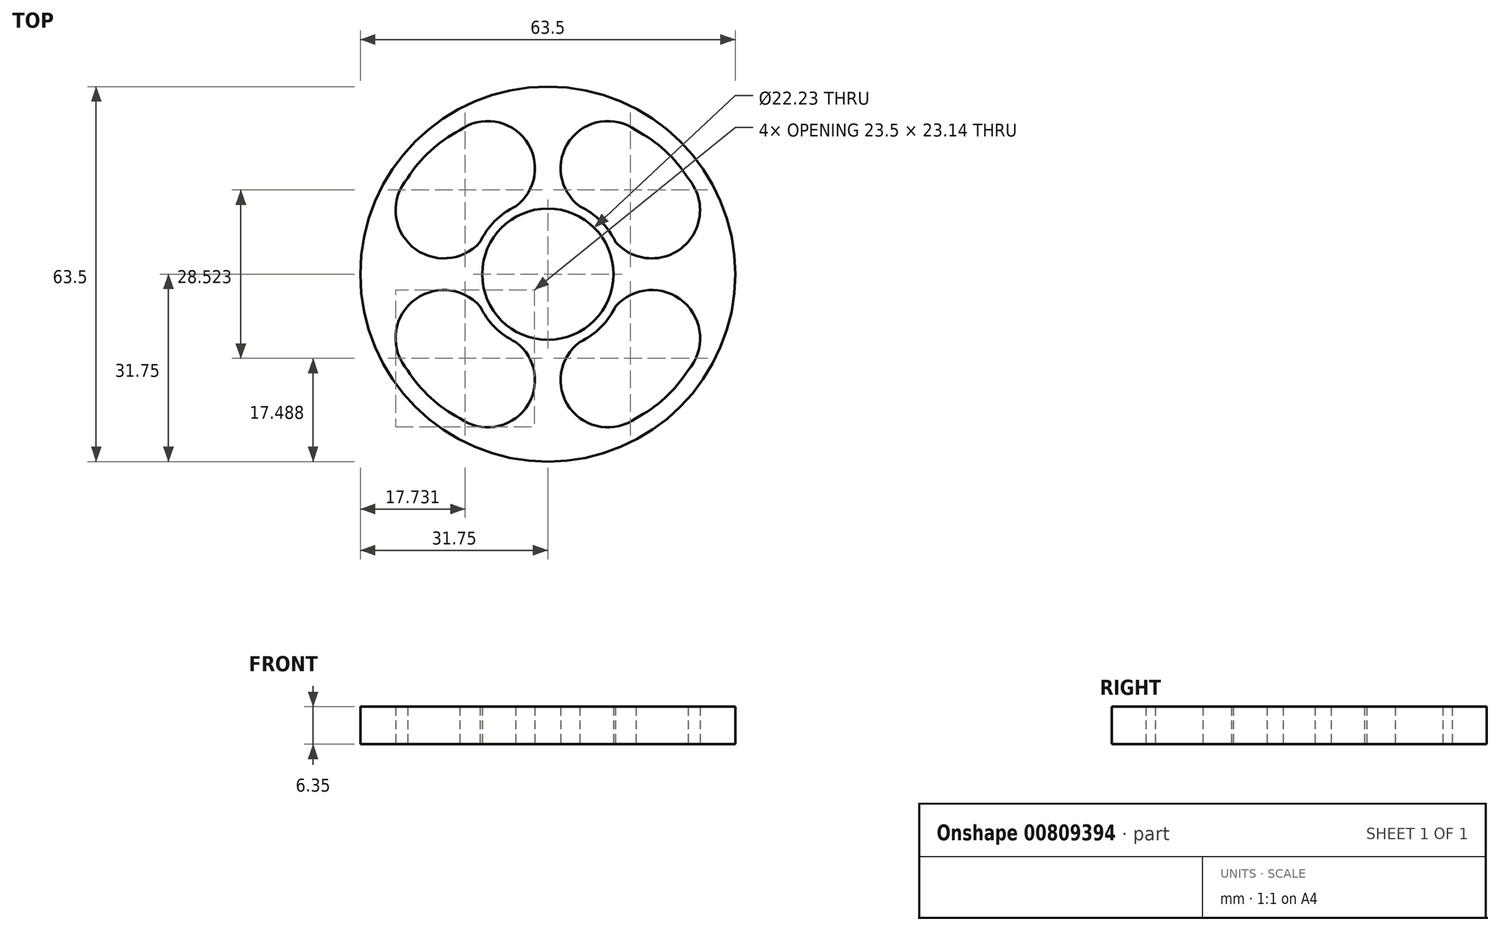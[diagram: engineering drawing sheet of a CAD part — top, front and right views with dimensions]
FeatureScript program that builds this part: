
annotation { "Feature Type Name" : "Feature", "Feature Type Description" : "" }
export const myFeature = defineFeature(function(context is Context, id is Id, definition is map)
    precondition{}
    {
        {
            var Q0;
            Q0=qCreatedBy(makeId("Top.planeOp"),FACE);
            var sketch = newSketch(context, id + "F0", { "sketchPlane" : qUnion([Q0])});
            skCircle(sketch, "E0", {"center": v(0, 0) * mm, "radius": 31.75 * mm});
            skCircle(sketch, "E1", {"center": v(0, 0) * mm, "radius": 11.11 * mm});
            skSolve(sketch);
        }
        {
            var Q0;
            Q0=makeQuery(id+"F0.imprint","IMPRINT",FACE,{"disambiguationData":[TD([[makeQuery(id+"F0.imprint","IMPRINT",EDGE,{"derivedFrom":sQuery(id+"F0.wireOp",EDGE,"E0")}),1.0]])]});
            extrude(context, id + "F1", {"entities" : qUnion([Q0]), "depth" : 6.35 * mm, "offsetDistance" : 25.4 * mm});
        }
        {
            var Q0;
            Q0=qCreatedBy(makeId("Top.planeOp"),FACE);
            var sketch = newSketch(context, id + "F2", { "sketchPlane" : qUnion([Q0])});
            skArc(sketch, "E2.MirrorCS", {"start": v(14.92, 24.37) * mm, "mid": v(3.73, 22.66) * mm, "end": v(5.44, 11.47) * mm});
            skArc(sketch, "E3.MirrorCS", {"start": v(23.74, 16.26) * mm, "mid": v(23.02, 4.72) * mm, "end": v(11.47, 5.44) * mm});
            skArc(sketch, "E4.trimOffspring", {"start": v(11.47, 5.44) * mm, "mid": v(8.98, 8.98) * mm, "end": v(5.44, 11.47) * mm});
            skArc(sketch, "E5.trimOffspring", {"start": v(23.74, 16.26) * mm, "mid": v(19.87, 20.9) * mm, "end": v(14.92, 24.37) * mm});
            skArc(sketch, "E6.MirrorCS", {"start": v(23.74, -16.26) * mm, "mid": v(23.02, -4.72) * mm, "end": v(11.47, -5.44) * mm});
            skArc(sketch, "E7.MirrorCS", {"start": v(23.74, -16.26) * mm, "mid": v(19.87, -20.9) * mm, "end": v(14.92, -24.37) * mm});
            skArc(sketch, "E8.MirrorCS", {"start": v(14.92, -24.37) * mm, "mid": v(3.73, -22.66) * mm, "end": v(5.44, -11.47) * mm});
            skArc(sketch, "E9.MirrorCS", {"start": v(11.47, -5.44) * mm, "mid": v(8.98, -8.98) * mm, "end": v(5.44, -11.47) * mm});
            skArc(sketch, "E10.MirrorCS", {"start": v(-14.92, 24.37) * mm, "mid": v(-3.73, 22.66) * mm, "end": v(-5.44, 11.47) * mm});
            skArc(sketch, "E11.MirrorCS", {"start": v(-11.47, 5.44) * mm, "mid": v(-8.98, 8.98) * mm, "end": v(-5.44, 11.47) * mm});
            skArc(sketch, "E12.MirrorCS", {"start": v(-23.74, 16.26) * mm, "mid": v(-23.02, 4.72) * mm, "end": v(-11.47, 5.44) * mm});
            skArc(sketch, "E13.MirrorCS", {"start": v(-23.74, 16.26) * mm, "mid": v(-19.87, 20.9) * mm, "end": v(-14.92, 24.37) * mm});
            skArc(sketch, "E14.MirrorCS", {"start": v(-11.47, -5.44) * mm, "mid": v(-8.98, -8.98) * mm, "end": v(-5.44, -11.47) * mm});
            skArc(sketch, "E15.MirrorCS", {"start": v(-23.74, -16.26) * mm, "mid": v(-23.02, -4.72) * mm, "end": v(-11.47, -5.44) * mm});
            skArc(sketch, "E16.MirrorCS", {"start": v(-23.74, -16.26) * mm, "mid": v(-19.87, -20.9) * mm, "end": v(-14.92, -24.37) * mm});
            skArc(sketch, "E17.MirrorCS", {"start": v(-14.92, -24.37) * mm, "mid": v(-3.73, -22.66) * mm, "end": v(-5.44, -11.47) * mm});
            skSolve(sketch);
        }
        {
            var Q0;
            Q0 = qSketchRegion(id + "F2", true);
            extrude(context, id + "F3", {"entities" : qUnion([Q0]), "operationType" : NewBodyOperationType.REMOVE, "endBound" : BoundingType.THROUGH_ALL, "depth" : 25.4 * mm, "offsetDistance" : 25.4 * mm});
        }
    });
